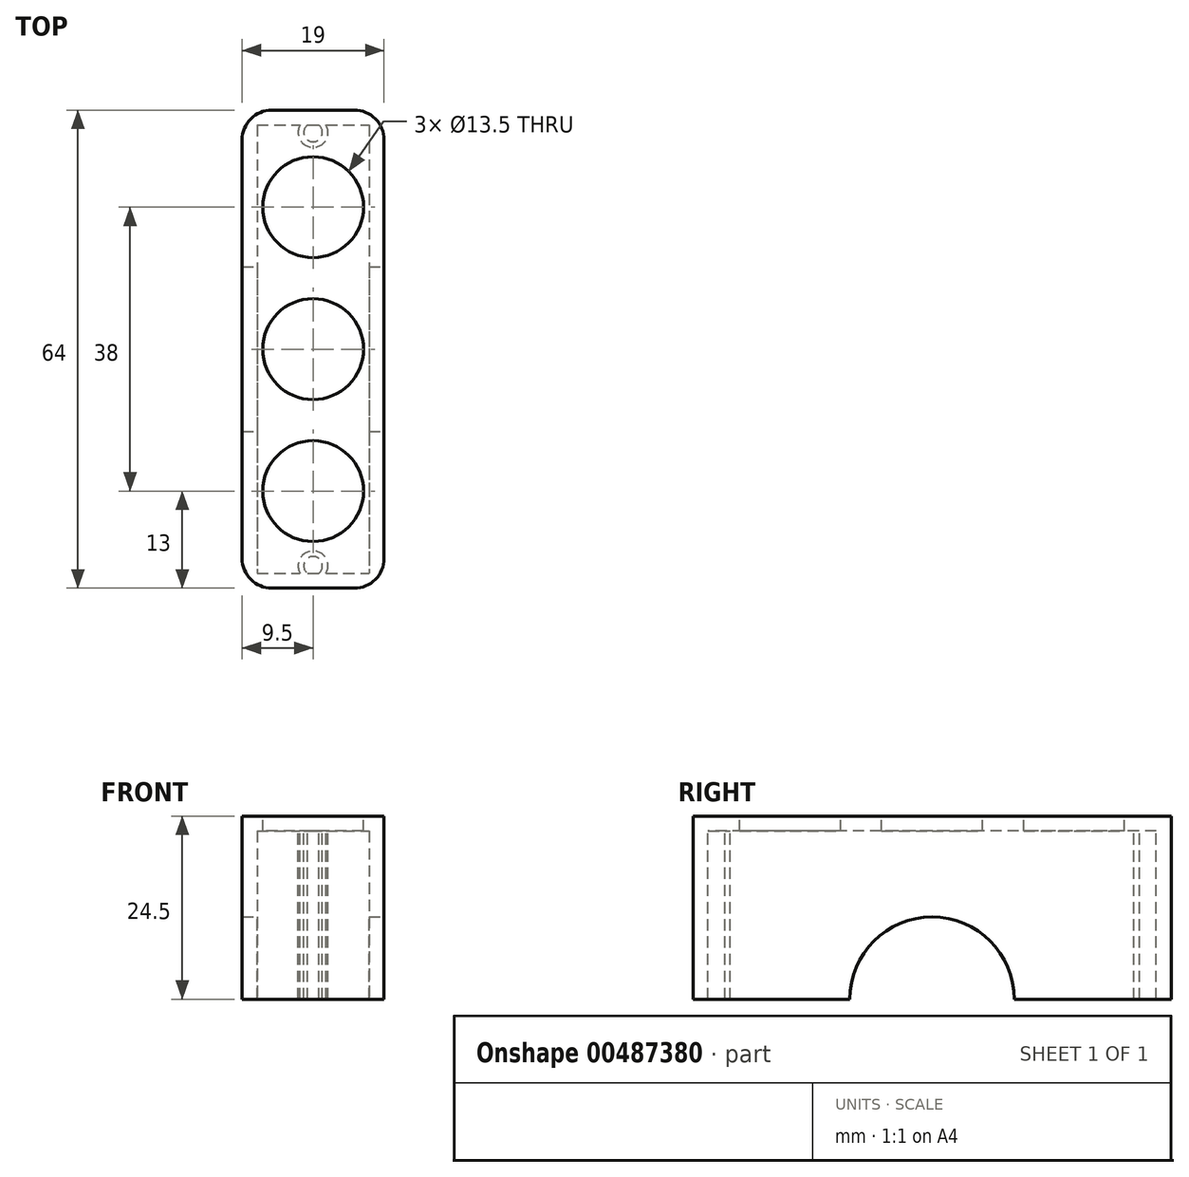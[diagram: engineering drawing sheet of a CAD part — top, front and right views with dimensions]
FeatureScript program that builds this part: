
annotation { "Feature Type Name" : "Feature", "Feature Type Description" : "" }
export const myFeature = defineFeature(function(context is Context, id is Id, definition is map)
    precondition{}
    {
        {
            var Q0;
            Q0=qCreatedBy(makeId("Top.planeOp"),FACE);
            var sketch = newSketch(context, id + "F0", { "sketchPlane" : qUnion([Q0])});
            skLineSegment(sketch, "E0.bottom", {"start": v(-19, 64) * mm, "end": v(0, 64) * mm});
            skLineSegment(sketch, "E0.top", {"start": v(-19, 0) * mm, "end": v(0, 0) * mm});
            skLineSegment(sketch, "E0.left", {"start": v(-19, 64) * mm, "end": v(-19, 0) * mm});
            skLineSegment(sketch, "E0.right", {"start": v(0, 64) * mm, "end": v(0, 0) * mm});
            skSolve(sketch);
        }
        {
            var Q0;
            Q0=qSketchRegion(id+"F0",true);
            extrude(context, id + "F1", {"entities" : qUnion([Q0]), "depth" : 24.5 * mm, "offsetDistance" : 25 * mm});
        }
        {
            var Q0;
            Q0=makeQuery(id+"F1.opExtrude","SWEPT_FACE",FACE,{"disambiguationData":[OSD([sQuery(id+"F0.wireOp",EDGE,"E0.right")])]});
            var sketch = newSketch(context, id + "F2", { "sketchPlane" : qUnion([Q0])});
            skArc(sketch, "E1", {"start": v(43, 0) * mm, "mid": v(32, 11) * mm, "end": v(21, 0) * mm});
            skLineSegment(sketch, "E2", {"start": v(21, 0) * mm, "end": v(43, 0) * mm});
            skSolve(sketch);
        }
        {
            var Q0;
            Q0=qSketchRegion(id+"F2",true);
            extrude(context, id + "F3", {"entities" : qUnion([Q0]), "operationType" : NewBodyOperationType.REMOVE, "oppositeDirection" : true, "depth" : 25 * mm});
        }
        {
            var Q0;
            Q0=makeQuery(id+"F3.boolean.opBoolean","COPY",FACE,{"derivedFrom":makeQuery(id+"F3.opExtrude","SWEPT_FACE",FACE,{"disambiguationData":[OSD([sQuery(id+"F2.wireOp",EDGE,"E1")])]})});
            var Q1;
            {var subQ0=sQuery(id+"F0.wireOp",EDGE,"E0.top");var subQ1=sQuery(id+"F0.wireOp",EDGE,"E0.left");var subQ2=sQuery(id+"F0.wireOp",EDGE,"E0.right");Q1=makeQuery(id+"F3.boolean.opBoolean","SPLIT",FACE,{"disambiguationData":[TD([makeQuery(id+"F1.opExtrude","SWEPT_FACE",FACE,{"disambiguationData":[OSD([subQ0])]})])],"derivedFrom":makeQuery(id+"F1.opExtrude","CAP_FACE",FACE,{"disambiguationData":[OSD([sQuery(id+"F0.wireOp",EDGE,"E0.bottom"),subQ0,subQ1,subQ2])],"isStart":true})});}
            var Q2;
            {var subQ0=sQuery(id+"F0.wireOp",EDGE,"E0.bottom");var subQ1=sQuery(id+"F0.wireOp",EDGE,"E0.right");var subQ2=sQuery(id+"F0.wireOp",EDGE,"E0.left");Q2=makeQuery(id+"F3.boolean.opBoolean","SPLIT",FACE,{"disambiguationData":[TD([makeQuery(id+"F1.opExtrude","SWEPT_FACE",FACE,{"disambiguationData":[OSD([subQ0])]})])],"derivedFrom":makeQuery(id+"F1.opExtrude","CAP_FACE",FACE,{"disambiguationData":[OSD([subQ0,sQuery(id+"F0.wireOp",EDGE,"E0.top"),subQ2,subQ1])],"isStart":true})});}
            shell(context, id + "F4", {"entities" : qUnion([Q0, Q1, Q2]), "thickness" : 2 * mm});
        }
        {
            var Q0;
            Q0=makeQuery(id+"F1.opExtrude","SWEPT_EDGE",EDGE,{"disambiguationData":[OSD([sQuery(id+"F0.wireOp",EDGE,"E0.top"),sQuery(id+"F0.wireOp",EDGE,"E0.right")])]});
            var Q1;
            Q1=makeQuery(id+"F1.opExtrude","SWEPT_EDGE",EDGE,{"disambiguationData":[OSD([sQuery(id+"F0.wireOp",EDGE,"E0.bottom"),sQuery(id+"F0.wireOp",EDGE,"E0.right")])]});
            var Q2;
            Q2=makeQuery(id+"F1.opExtrude","SWEPT_EDGE",EDGE,{"disambiguationData":[OSD([sQuery(id+"F0.wireOp",EDGE,"E0.bottom"),sQuery(id+"F0.wireOp",EDGE,"E0.left")])]});
            var Q3;
            Q3=makeQuery(id+"F1.opExtrude","SWEPT_EDGE",EDGE,{"disambiguationData":[OSD([sQuery(id+"F0.wireOp",EDGE,"E0.top"),sQuery(id+"F0.wireOp",EDGE,"E0.left")])]});
            fillet(context, id + "F5", {"entities" : qUnion([Q0, Q1, Q2, Q3]), "radius" : 4 * mm, "tangentPropagation" : true, "defaultsChanged" : false, "vertexSettings" : [], "allowEdgeOverflow" : false});
        }
        {
            var Q0;
            Q0=makeQuery(id+"F1.opExtrude","CAP_FACE",FACE,{"disambiguationData":[OSD([sQuery(id+"F0.wireOp",EDGE,"E0.bottom"),sQuery(id+"F0.wireOp",EDGE,"E0.top"),sQuery(id+"F0.wireOp",EDGE,"E0.left"),sQuery(id+"F0.wireOp",EDGE,"E0.right")])],"isStart":false});
            var sketch = newSketch(context, id + "F6", { "sketchPlane" : qUnion([Q0])});
            skCircle(sketch, "E3", {"center": v(-9.5, 32) * mm, "radius": 6.75 * mm});
            skPoint(sketch, "E3.centerSnap0", {"position": v(-19, 32) * mm});
            skSolve(sketch);
        }
        {
            var Q0;
            Q0=qSketchRegion(id+"F6",true);
            extrude(context, id + "F7", {"entities" : qUnion([Q0]), "operationType" : NewBodyOperationType.REMOVE, "oppositeDirection" : true, "depth" : 25 * mm});
        }
        {
            var Q0;
            Q0=makeQuery(id+"F4.opShell","OFFSET_FACE",FACE,{"disambiguationData":[OSD([sQuery(id+"F0.wireOp",EDGE,"E0.bottom"),sQuery(id+"F0.wireOp",EDGE,"E0.top"),sQuery(id+"F0.wireOp",EDGE,"E0.left"),sQuery(id+"F0.wireOp",EDGE,"E0.right")])]});
            var sketch = newSketch(context, id + "F8", { "sketchPlane" : qUnion([Q0])});
            skCircle(sketch, "E4", {"center": v(-9.5, -3) * mm, "radius": 2 * mm});
            skCircle(sketch, "E5", {"center": v(-9.5, -3) * mm, "radius": 1.25 * mm});
            skLineSegment(sketch, "E6", {"start": v(-17, -32) * mm, "end": v(-2, -32) * mm, "construction": true});
            skCircle(sketch, "E7.MirrorC", {"center": v(-9.5, -61) * mm, "radius": 2 * mm});
            skCircle(sketch, "E8.MirrorC", {"center": v(-9.5, -61) * mm, "radius": 1.25 * mm});
            skSolve(sketch);
        }
        {
            var Q0;
            Q0=qSketchRegion(id+"F8",true);
            extrude(context, id + "F9", {"entities" : qUnion([Q0]), "operationType" : NewBodyOperationType.ADD, "depth" : 22.5 * mm, "offsetDistance" : 25 * mm});
        }
        {
            var Q0;
            {var subQ0=sQuery(id+"F0.wireOp",EDGE,"E0.left");var subQ1=sQuery(id+"F0.wireOp",EDGE,"E0.bottom");var subQ2=sQuery(id+"F0.wireOp",EDGE,"E0.right");Q0=makeQuery(id+"FS9lYY6Vs6I1Vlx_1.boolean.opBoolean","SPLIT",FACE,{"disambiguationData":[TD([makeQuery(id+"F1.opExtrude","SWEPT_FACE",FACE,{"disambiguationData":[OSD([subQ1])]})])],"derivedFrom":makeQuery(id+"F1.opExtrude","CAP_FACE",FACE,{"disambiguationData":[OSD([subQ1,sQuery(id+"F0.wireOp",EDGE,"E0.top"),subQ0,subQ2])],"isStart":false})});}
            var sketch = newSketch(context, id + "F10", { "sketchPlane" : qUnion([Q0])});
            skCircle(sketch, "E9", {"center": v(-9.5, 51) * mm, "radius": 6.75 * mm});
            skLineSegment(sketch, "E10", {"start": v(-19, 32) * mm, "end": v(0, 32) * mm, "construction": true});
            skCircle(sketch, "E11.MirrorC", {"center": v(-9.5, 13) * mm, "radius": 6.75 * mm});
            skSolve(sketch);
        }
        {
            var Q0;
            Q0 = qSketchRegion(id + "F10", true);
            extrude(context, id + "F11", {"entities" : qUnion([Q0]), "operationType" : NewBodyOperationType.REMOVE, "oppositeDirection" : true, "depth" : 25 * mm});
        }
    });
